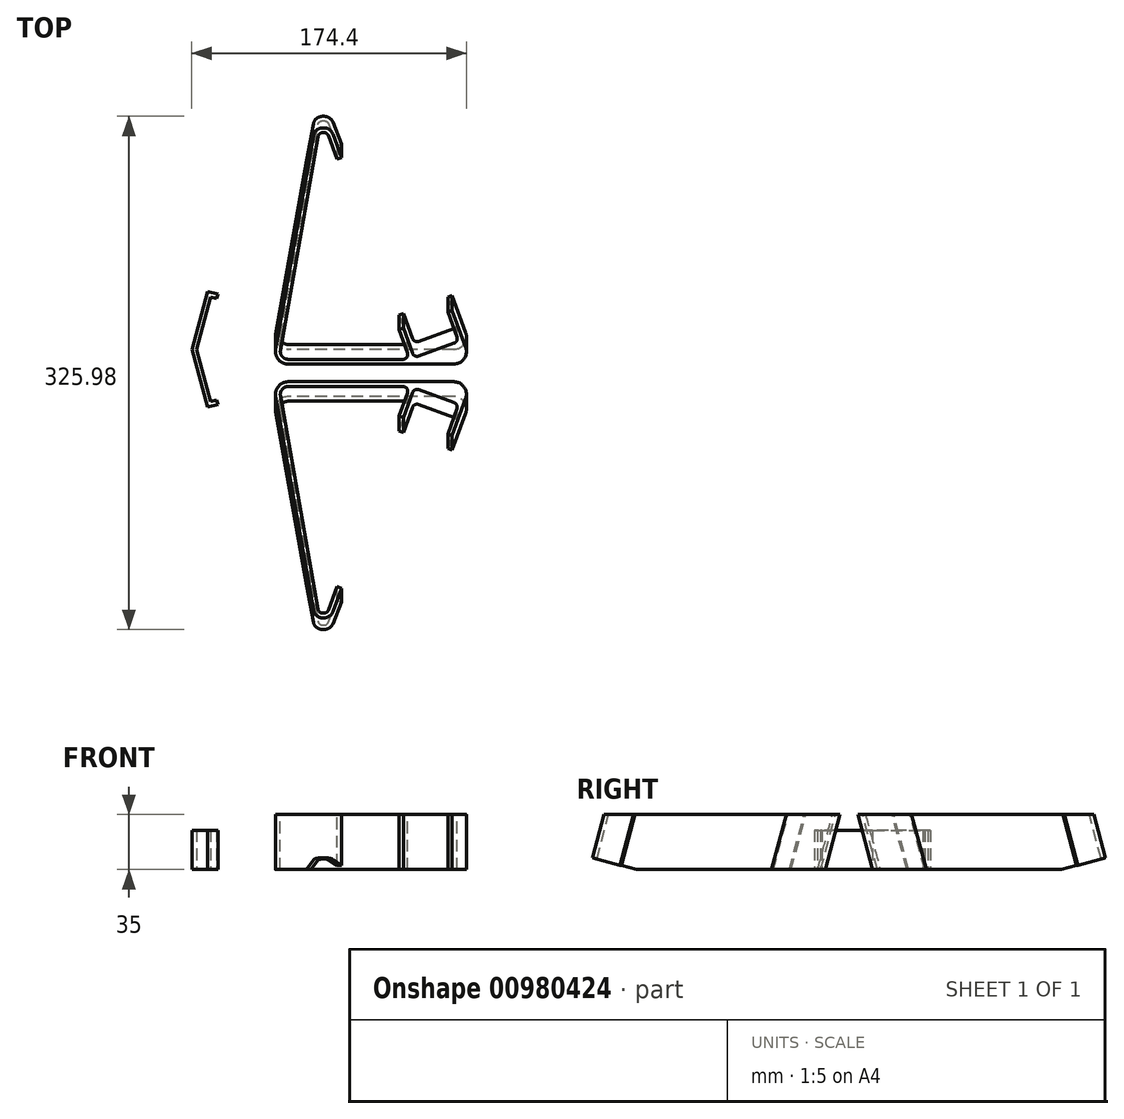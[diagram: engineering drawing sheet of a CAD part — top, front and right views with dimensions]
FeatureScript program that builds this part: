
annotation { "Feature Type Name" : "Feature", "Feature Type Description" : "" }
export const myFeature = defineFeature(function(context is Context, id is Id, definition is map)
    precondition{}
    {
        {
            var Q0;
            Q0=qCreatedBy(makeId("Top.planeOp"),FACE);
            var sketch = newSketch(context, id + "F0", { "sketchPlane" : qUnion([Q0])});
            skLineSegment(sketch, "E0", {"start": v(56.29, 22.82) * mm, "end": v(62.1, 6.85) * mm});
            skLineSegment(sketch, "E1", {"start": v(65.95, 5.05) * mm, "end": v(88.5, 13.26) * mm});
            skLineSegment(sketch, "E2", {"start": v(90.3, 17.1) * mm, "end": v(84.48, 33.08) * mm});
            skLineSegment(sketch, "E3", {"start": v(84.48, 33.08) * mm, "end": v(87.3, 34.1) * mm});
            skLineSegment(sketch, "E4", {"start": v(87.3, 34.1) * mm, "end": v(95.8, 10.74) * mm});
            skLineSegment(sketch, "E5", {"start": v(88.29, 0) * mm, "end": v(-16.92, 0) * mm});
            skLineSegment(sketch, "E6", {"start": v(-24.8, 9.39) * mm, "end": v(-0.87, 145.04) * mm});
            skLineSegment(sketch, "E7", {"start": v(5.03, 150) * mm, "end": v(5.8, 150) * mm});
            skLineSegment(sketch, "E8", {"start": v(11.44, 146.05) * mm, "end": v(16.84, 131.2) * mm});
            skLineSegment(sketch, "E9", {"start": v(56.29, 22.82) * mm, "end": v(16.84, 131.2) * mm, "construction": true});
            skLineSegment(sketch, "E10.0", {"start": v(8.62, 145.03) * mm, "end": v(14.02, 130.18) * mm});
            skLineSegment(sketch, "E10.1", {"start": v(5.03, 147) * mm, "end": v(5.8, 147) * mm});
            skLineSegment(sketch, "E10.2", {"start": v(-21.84, 8.87) * mm, "end": v(2.08, 144.52) * mm});
            skLineSegment(sketch, "E10.3", {"start": v(53.47, 21.8) * mm, "end": v(58.85, 7.03) * mm});
            skLineSegment(sketch, "E10.6", {"start": v(56.03, 3) * mm, "end": v(-16.92, 3) * mm});
            skLineSegment(sketch, "E11", {"start": v(53.47, 21.8) * mm, "end": v(56.29, 22.82) * mm});
            skLineSegment(sketch, "E12", {"start": v(14.02, 130.18) * mm, "end": v(16.84, 131.2) * mm});
            skLineSegment(sketch, "E13", {"start": v(56.29, 22.82) * mm, "end": v(84.48, 33.08) * mm, "construction": true});
            skPoint(sketch, "E14.visualSharp", {"position": v(-26.45, 0) * mm});
            skArc(sketch, "E14.filletArc", {"start": v(-24.8, 9.39) * mm, "mid": v(-23.04, 2.86) * mm, "end": v(-16.92, 0) * mm});
            skPoint(sketch, "E15.visualSharp", {"position": v(-22.87, 3) * mm});
            skArc(sketch, "E15.filletArc", {"start": v(-21.84, 8.87) * mm, "mid": v(-20.75, 4.79) * mm, "end": v(-16.92, 3) * mm});
            skPoint(sketch, "E16.visualSharp", {"position": v(95.43, 3) * mm});
            skPoint(sketch, "E17.visualSharp", {"position": v(99.71, 0) * mm});
            skArc(sketch, "E17.filletArc", {"start": v(88.29, 0) * mm, "mid": v(94.84, 3.41) * mm, "end": v(95.8, 10.74) * mm});
            skLineSegment(sketch, "E18", {"start": v(60.31, 3) * mm, "end": v(63.13, 4.03) * mm, "construction": true});
            skPoint(sketch, "E19.visualSharp", {"position": v(2.52, 147) * mm});
            skArc(sketch, "E19.filletArc", {"start": v(5.03, 147) * mm, "mid": v(3.1, 146.3) * mm, "end": v(2.08, 144.52) * mm});
            skPoint(sketch, "E20.visualSharp", {"position": v(7.9, 147) * mm});
            skArc(sketch, "E20.filletArc", {"start": v(8.62, 145.03) * mm, "mid": v(7.52, 146.46) * mm, "end": v(5.8, 147) * mm});
            skPoint(sketch, "E21.visualSharp", {"position": v(0, 150) * mm});
            skArc(sketch, "E21.filletArc", {"start": v(5.03, 150) * mm, "mid": v(1.18, 148.6) * mm, "end": v(-0.87, 145.04) * mm});
            skPoint(sketch, "E22.visualSharp", {"position": v(10, 150) * mm});
            skArc(sketch, "E22.filletArc", {"start": v(11.44, 146.05) * mm, "mid": v(9.24, 148.91) * mm, "end": v(5.8, 150) * mm});
            skPoint(sketch, "E23.visualSharp", {"position": v(60.31, 3) * mm});
            skArc(sketch, "E23.filletArc", {"start": v(56.03, 3) * mm, "mid": v(58.48, 4.28) * mm, "end": v(58.85, 7.03) * mm});
            skPoint(sketch, "E24.visualSharp", {"position": v(63.13, 4.03) * mm});
            skArc(sketch, "E24.filletArc", {"start": v(62.1, 6.85) * mm, "mid": v(63.66, 5.15) * mm, "end": v(65.95, 5.05) * mm});
            skPoint(sketch, "E25.visualSharp", {"position": v(91.32, 14.29) * mm});
            skArc(sketch, "E25.filletArc", {"start": v(88.5, 13.26) * mm, "mid": v(90.2, 14.81) * mm, "end": v(90.3, 17.1) * mm});
            skSolve(sketch);
        }
        {
            var Q0;
            Q0=qCreatedBy(makeId("Right.planeOp"),FACE);
            var sketch = newSketch(context, id + "F1", { "sketchPlane" : qUnion([Q0])});
            skLineSegment(sketch, "E26", {"start": v(0, 0) * mm, "end": v(-9.38, 35) * mm});
            skLineSegment(sketch, "E27", {"start": v(0, 0) * mm, "end": v(-9.38, 0) * mm, "construction": true});
            skLineSegment(sketch, "E28", {"start": v(-9.38, 0) * mm, "end": v(-9.38, 35) * mm, "construction": true});
            skPoint(sketch, "E29.0", {"position": v(120, 0) * mm});
            skPoint(sketch, "E30.0", {"position": v(150, 0) * mm});
            skLineSegment(sketch, "E31", {"start": v(120, 0) * mm, "end": v(150, 8.04) * mm});
            skLineSegment(sketch, "E32", {"start": v(120, 0) * mm, "end": v(122.59, -9.66) * mm});
            skLineSegment(sketch, "E33", {"start": v(122.59, -9.66) * mm, "end": v(152.59, -1.62) * mm});
            skLineSegment(sketch, "E34", {"start": v(152.59, -1.62) * mm, "end": v(150, 8.04) * mm});
            skSolve(sketch);
        }
        {
            var Q0;
            Q0=makeQuery(id+"F0.imprint","IMPRINT",FACE,{"disambiguationData":[TD([[makeQuery(id+"F0.imprint","IMPRINT",EDGE,{"derivedFrom":sQuery(id+"F0.wireOp",EDGE,"E0")}),-1.0]])]});
            var Q1;
            Q1=sQuery(id+"F1.wireOp",EDGE,"E26");
            sweep(context, id + "F2", {"profiles" : qUnion([Q0]), "path" : qUnion([Q1])});
        }
        {
            var Q0;
            Q0=makeQuery(id+"F1.imprint","IMPRINT",FACE,{"disambiguationData":[TD([[makeQuery(id+"F1.imprint","IMPRINT",EDGE,{"derivedFrom":sQuery(id+"F1.wireOp",EDGE,"E31")}),-1.0]])]});
            extrude(context, id + "F3", {"entities" : qUnion([Q0]), "operationType" : NewBodyOperationType.REMOVE, "endBound" : BoundingType.THROUGH_ALL, "oppositeDirection" : true, "depth" : 25 * mm, "offsetDistance" : 25 * mm, "hasSecondDirection" : true, "secondDirectionBound" : SecondDirectionBoundingType.THROUGH_ALL, "secondDirectionOppositeDirection" : false, "secondDirectionDepth" : 25 * mm});
        }
        {
            var Q0;
            Q0=makeQuery(id+"F2.opSweep","SWEPT_BODY",BODY,{"disambiguationData":[OSD([sQuery(id+"F0.wireOp",EDGE,"E0"),sQuery(id+"F0.wireOp",EDGE,"E1"),sQuery(id+"F0.wireOp",EDGE,"E2"),sQuery(id+"F0.wireOp",EDGE,"E3"),sQuery(id+"F0.wireOp",EDGE,"E4"),sQuery(id+"F0.wireOp",EDGE,"E5"),sQuery(id+"F0.wireOp",EDGE,"E6"),sQuery(id+"F0.wireOp",EDGE,"E7"),sQuery(id+"F0.wireOp",EDGE,"E8"),sQuery(id+"F0.wireOp",EDGE,"E10.0"),sQuery(id+"F0.wireOp",EDGE,"E10.1"),sQuery(id+"F0.wireOp",EDGE,"E10.2"),sQuery(id+"F0.wireOp",EDGE,"E10.3"),sQuery(id+"F0.wireOp",EDGE,"E10.6"),sQuery(id+"F0.wireOp",EDGE,"E11"),sQuery(id+"F0.wireOp",EDGE,"E12"),sQuery(id+"F0.wireOp",EDGE,"E14.filletArc"),sQuery(id+"F0.wireOp",EDGE,"E15.filletArc"),sQuery(id+"F0.wireOp",EDGE,"E17.filletArc"),sQuery(id+"F0.wireOp",EDGE,"E19.filletArc"),sQuery(id+"F0.wireOp",EDGE,"E20.filletArc"),sQuery(id+"F0.wireOp",EDGE,"E21.filletArc"),sQuery(id+"F0.wireOp",EDGE,"E22.filletArc"),sQuery(id+"F0.wireOp",EDGE,"E23.filletArc"),sQuery(id+"F0.wireOp",EDGE,"E24.filletArc"),sQuery(id+"F0.wireOp",EDGE,"E25.filletArc"),sQuery(id+"F1.wireOp",EDGE,"E26")])]});
            var Q1;
            Q1=qCreatedBy(makeId("Front.planeOp"),FACE);
            mirror(context, id + "F4", {"entities" : qUnion([Q0]), "mirrorPlane" : qUnion([Q1])});
        }
        {
            var Q0;
            Q0=makeQuery(id+"F4.opPattern","COPY",BODY,{"derivedFrom":makeQuery(id+"F2.opSweep","SWEPT_BODY",BODY,{"disambiguationData":[OSD([sQuery(id+"F0.wireOp",EDGE,"E0"),sQuery(id+"F0.wireOp",EDGE,"E1"),sQuery(id+"F0.wireOp",EDGE,"E2"),sQuery(id+"F0.wireOp",EDGE,"E3"),sQuery(id+"F0.wireOp",EDGE,"E4"),sQuery(id+"F0.wireOp",EDGE,"E5"),sQuery(id+"F0.wireOp",EDGE,"E6"),sQuery(id+"F0.wireOp",EDGE,"E7"),sQuery(id+"F0.wireOp",EDGE,"E8"),sQuery(id+"F0.wireOp",EDGE,"E10.0"),sQuery(id+"F0.wireOp",EDGE,"E10.1"),sQuery(id+"F0.wireOp",EDGE,"E10.2"),sQuery(id+"F0.wireOp",EDGE,"E10.3"),sQuery(id+"F0.wireOp",EDGE,"E10.6"),sQuery(id+"F0.wireOp",EDGE,"E11"),sQuery(id+"F0.wireOp",EDGE,"E12"),sQuery(id+"F0.wireOp",EDGE,"E14.filletArc"),sQuery(id+"F0.wireOp",EDGE,"E15.filletArc"),sQuery(id+"F0.wireOp",EDGE,"E17.filletArc"),sQuery(id+"F0.wireOp",EDGE,"E19.filletArc"),sQuery(id+"F0.wireOp",EDGE,"E20.filletArc"),sQuery(id+"F0.wireOp",EDGE,"E21.filletArc"),sQuery(id+"F0.wireOp",EDGE,"E22.filletArc"),sQuery(id+"F0.wireOp",EDGE,"E23.filletArc"),sQuery(id+"F0.wireOp",EDGE,"E24.filletArc"),sQuery(id+"F0.wireOp",EDGE,"E25.filletArc"),sQuery(id+"F1.wireOp",EDGE,"E26")])]}),"instanceName":"1"});
            transform(context, id + "F5", {"entities" : qUnion([Q0]), "transformType" : TransformType.TRANSLATION_3D, "dx" : 0 * mm, "dy" : -30 * mm, "dz" : 0 * mm, "makeCopy" : false});
        }
        {
            var Q0;
            Q0=qCreatedBy(makeId("Top.planeOp"),FACE);
            var sketch = newSketch(context, id + "F6", { "sketchPlane" : qUnion([Q0])});
            skLineSegment(sketch, "E35", {"start": v(-78.1, 0) * mm, "end": v(-68.24, 36.81) * mm});
            skLineSegment(sketch, "E36", {"start": v(-68.24, 36.81) * mm, "end": v(-65.34, 36.04) * mm});
            skLineSegment(sketch, "E37", {"start": v(-66.12, 33.14) * mm, "end": v(-75, 0) * mm});
            skLineSegment(sketch, "E38", {"start": v(-65.34, 36.04) * mm, "end": v(-61.48, 35) * mm});
            skLineSegment(sketch, "E39", {"start": v(-61.48, 35) * mm, "end": v(-62.26, 32.1) * mm});
            skLineSegment(sketch, "E40", {"start": v(-62.26, 32.1) * mm, "end": v(-66.12, 33.14) * mm});
            skLineSegment(sketch, "E41", {"start": v(-78.1, 0) * mm, "end": v(-75, 0) * mm, "construction": true});
            skLineSegment(sketch, "E42.MirrorCS", {"start": v(-78.1, 0) * mm, "end": v(-68.24, -36.81) * mm});
            skLineSegment(sketch, "E43.MirrorCS", {"start": v(-66.12, -33.14) * mm, "end": v(-75, 0) * mm});
            skLineSegment(sketch, "E44.MirrorCS", {"start": v(-68.24, -36.81) * mm, "end": v(-65.34, -36.04) * mm});
            skLineSegment(sketch, "E45.MirrorCS", {"start": v(-65.34, -36.04) * mm, "end": v(-61.48, -35) * mm});
            skLineSegment(sketch, "E46.MirrorCS", {"start": v(-61.48, -35) * mm, "end": v(-62.26, -32.1) * mm});
            skLineSegment(sketch, "E47.MirrorCS", {"start": v(-62.26, -32.1) * mm, "end": v(-66.12, -33.14) * mm});
            skSolve(sketch);
        }
        {
            var Q0;
            Q0=makeQuery(id+"F6.imprint","IMPRINT",FACE,{"disambiguationData":[TD([[makeQuery(id+"F6.imprint","IMPRINT",EDGE,{"derivedFrom":sQuery(id+"F6.wireOp",EDGE,"E35")}),-1.0]])]});
            extrude(context, id + "F7", {"entities" : qUnion([Q0]), "depth" : 25 * mm, "offsetDistance" : 25 * mm});
        }
    });
